# Revit family: Robe_Hook-American_Standard-Studio_S-7105.210
name_source: partatom
category: Specialty Equipment
revit_build: Autodesk Revit 2018 (Build: 20170223_1515(x64)
units: mm (PartAtom-declared; Revit-internal decimal feet)

## family parameters
Cut with Voids When Loaded = No
Host = Face
OmniClass Number = 23.40.20.21.31
OmniClass Title = Robe Hooks
Part Type = Normal
Room Calculation Point = No
Round Connector Dimension = Use Diameter
Shared = Yes

## types (3) — shared parameters
Assembly Code = C1030220
Default Elevation = 60"
Description = Studio S Double Bath Accessories Robe Hook
Height = 4 1/16"
Installation Type = Wall Mounted
Length = 1 5/8"
Manufacturer = American Standard
Price = Prices may vary. Please consult Manufacturer Representative for most up-to-date price list.
Product Documentation Link = https://www.americanstandard-us.com
Product Page URL = https://www.americanstandard-us.com
Revised Date = 05/03/2021
URL = https://www.americanstandard-us.com
Warranty Information = One Year General Product Warranty
Width = 2 15/16"

## per-type parameters (varying)
| type | Finish | Material |
| 7105.210.002 | Metal-American_Standard-002-Polished_Chrome | Metal-American_Standard-002-Polished_Chrome |
| 7105.210.295 | Metal-American_Standard-295-Brushed_Nickel | Metal-American_Standard-295-Brushed_Nickel |
| 7105.210.243 | Metal-American_Standard-243-Matte_Black | Metal-American_Standard-243-Matte_Black |

note: column(s) folded — value = type name in every type: Model

## geometry (parser evidence)
native form markers: Sweep x3
no freeform markers — native parametric forms only
